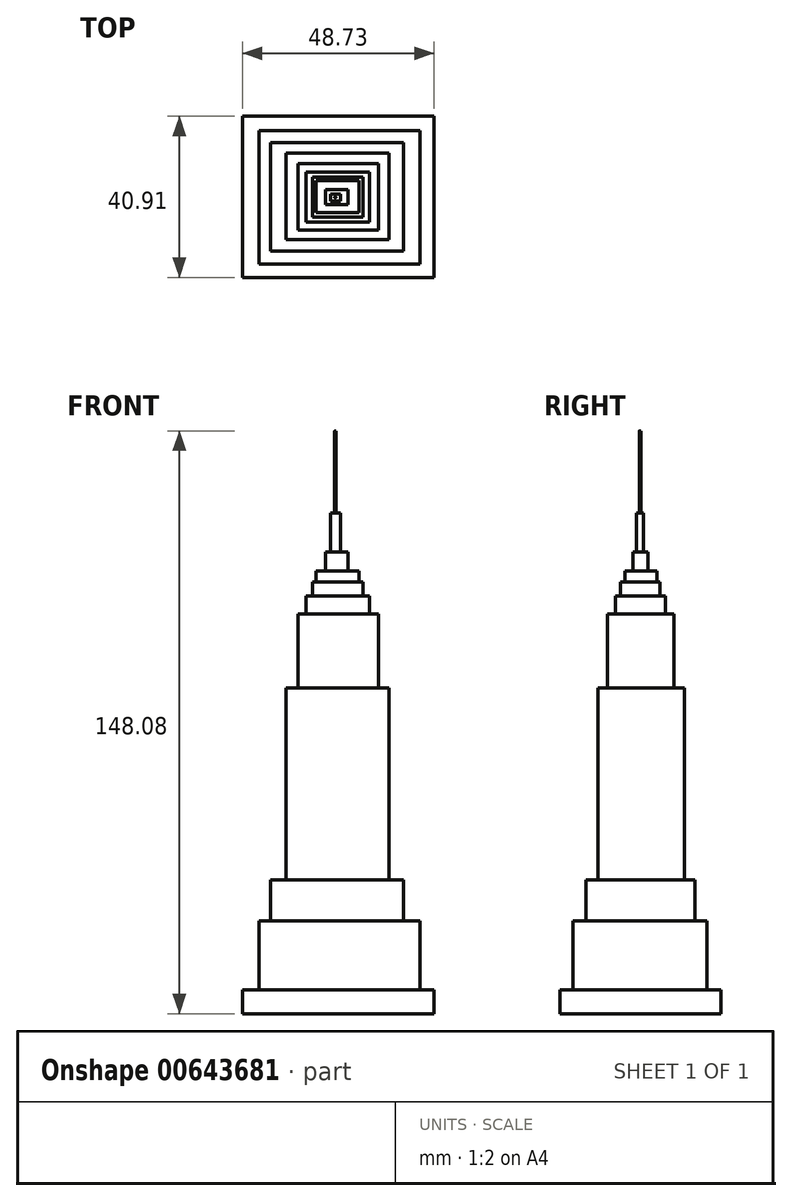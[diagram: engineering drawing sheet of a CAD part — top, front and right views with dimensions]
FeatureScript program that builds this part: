
annotation { "Feature Type Name" : "Feature", "Feature Type Description" : "" }
export const myFeature = defineFeature(function(context is Context, id is Id, definition is map)
    precondition{}
    {
        {
            var Q0;
            Q0=qCreatedBy(makeId("Top.planeOp"),FACE);
            var sketch = newSketch(context, id + "F0", { "sketchPlane" : qUnion([Q0])});
            skLineSegment(sketch, "E0.bottom", {"start": v(-23.61, 19.7) * mm, "end": v(25.12, 19.7) * mm});
            skLineSegment(sketch, "E0.top", {"start": v(-23.61, -21.2) * mm, "end": v(25.12, -21.2) * mm});
            skLineSegment(sketch, "E0.left", {"start": v(-23.61, 19.7) * mm, "end": v(-23.61, -21.2) * mm});
            skLineSegment(sketch, "E0.right", {"start": v(25.12, 19.7) * mm, "end": v(25.12, -21.2) * mm});
            skSolve(sketch);
        }
        {
            var Q0;
            Q0=makeQuery(id+"F0.imprint","IMPRINT",FACE,{"disambiguationData":[TD([[makeQuery(id+"F0.imprint","IMPRINT",EDGE,{"derivedFrom":sQuery(id+"F0.wireOp",EDGE,"E0.bottom")}),-1.0]])]});
            extrude(context, id + "F1", {"entities" : qUnion([Q0]), "depth" : 6.1 * mm, "offsetDistance" : 25.4 * mm});
        }
        {
            var Q0;
            Q0=makeQuery(id+"F1.opExtrude","CAP_FACE",FACE,{"disambiguationData":[OSD([sQuery(id+"F0.wireOp",EDGE,"E0.bottom"),sQuery(id+"F0.wireOp",EDGE,"E0.top"),sQuery(id+"F0.wireOp",EDGE,"E0.left"),sQuery(id+"F0.wireOp",EDGE,"E0.right")])],"isStart":false});
            var sketch = newSketch(context, id + "F2", { "sketchPlane" : qUnion([Q0])});
            skLineSegment(sketch, "E1.bottom", {"start": v(-19.4, 16.1) * mm, "end": v(21.5, 16.1) * mm});
            skLineSegment(sketch, "E1.top", {"start": v(-19.4, -17.9) * mm, "end": v(21.5, -17.9) * mm});
            skLineSegment(sketch, "E1.left", {"start": v(-19.4, 16.1) * mm, "end": v(-19.4, -17.9) * mm});
            skLineSegment(sketch, "E1.right", {"start": v(21.5, 16.1) * mm, "end": v(21.5, -17.9) * mm});
            skSolve(sketch);
        }
        {
            var Q0;
            Q0=makeQuery(id+"F2.imprint","IMPRINT",FACE,{"disambiguationData":[TD([[makeQuery(id+"F2.imprint","IMPRINT",EDGE,{"derivedFrom":sQuery(id+"F2.wireOp",EDGE,"E1.bottom")}),-1.0]])]});
            extrude(context, id + "F3", {"entities" : qUnion([Q0]), "depth" : 17.53 * mm, "offsetDistance" : 25.4 * mm});
        }
        {
            var Q0;
            Q0=makeQuery(id+"F3.opExtrude","CAP_FACE",FACE,{"disambiguationData":[OSD([sQuery(id+"F2.wireOp",EDGE,"E1.bottom"),sQuery(id+"F2.wireOp",EDGE,"E1.top"),sQuery(id+"F2.wireOp",EDGE,"E1.left"),sQuery(id+"F2.wireOp",EDGE,"E1.right")])],"isStart":false});
            var sketch = newSketch(context, id + "F4", { "sketchPlane" : qUnion([Q0])});
            skLineSegment(sketch, "E2.bottom", {"start": v(17.3, -14.59) * mm, "end": v(-16.4, -14.59) * mm});
            skLineSegment(sketch, "E2.top", {"start": v(17.3, 13.08) * mm, "end": v(-16.4, 13.08) * mm});
            skLineSegment(sketch, "E2.left", {"start": v(17.3, -14.59) * mm, "end": v(17.3, 13.08) * mm});
            skLineSegment(sketch, "E2.right", {"start": v(-16.4, -14.59) * mm, "end": v(-16.4, 13.08) * mm});
            skSolve(sketch);
        }
        {
            var Q0;
            Q0 = qSketchRegion(id + "F4", true);
            extrude(context, id + "F5", {"entities" : qUnion([Q0]), "depth" : 10.4 * mm, "offsetDistance" : 25.4 * mm});
        }
        {
            var Q0;
            Q0=makeQuery(id+"F5.opExtrude","CAP_FACE",FACE,{"disambiguationData":[OSD([sQuery(id+"F4.wireOp",EDGE,"E2.bottom"),sQuery(id+"F4.wireOp",EDGE,"E2.top"),sQuery(id+"F4.wireOp",EDGE,"E2.left"),sQuery(id+"F4.wireOp",EDGE,"E2.right")])],"isStart":false});
            var sketch = newSketch(context, id + "F6", { "sketchPlane" : qUnion([Q0])});
            skLineSegment(sketch, "E3.bottom", {"start": v(-12.48, 10.38) * mm, "end": v(13.69, 10.38) * mm});
            skLineSegment(sketch, "E3.top", {"start": v(-12.48, -11.58) * mm, "end": v(13.69, -11.58) * mm});
            skLineSegment(sketch, "E3.left", {"start": v(-12.48, 10.38) * mm, "end": v(-12.48, -11.58) * mm});
            skLineSegment(sketch, "E3.right", {"start": v(13.69, 10.38) * mm, "end": v(13.69, -11.58) * mm});
            skSolve(sketch);
        }
        {
            var Q0;
            Q0 = qSketchRegion(id + "F6", true);
            extrude(context, id + "F7", {"entities" : qUnion([Q0]), "depth" : 48.77 * mm, "offsetDistance" : 25.4 * mm});
        }
        {
            var Q0;
            Q0=makeQuery(id+"F7.opExtrude","CAP_FACE",FACE,{"disambiguationData":[OSD([sQuery(id+"F6.wireOp",EDGE,"E3.bottom"),sQuery(id+"F6.wireOp",EDGE,"E3.top"),sQuery(id+"F6.wireOp",EDGE,"E3.left"),sQuery(id+"F6.wireOp",EDGE,"E3.right")])],"isStart":false});
            var sketch = newSketch(context, id + "F8", { "sketchPlane" : qUnion([Q0])});
            skLineSegment(sketch, "E4.bottom", {"start": v(-9.47, 7.67) * mm, "end": v(10.98, 7.67) * mm});
            skLineSegment(sketch, "E4.top", {"start": v(-9.47, -9.17) * mm, "end": v(10.98, -9.17) * mm});
            skLineSegment(sketch, "E4.left", {"start": v(-9.47, 7.67) * mm, "end": v(-9.47, -9.17) * mm});
            skLineSegment(sketch, "E4.right", {"start": v(10.98, 7.67) * mm, "end": v(10.98, -9.17) * mm});
            skSolve(sketch);
        }
        {
            var Q0;
            Q0=makeQuery(id+"F8.imprint","IMPRINT",FACE,{"disambiguationData":[TD([[makeQuery(id+"F8.imprint","IMPRINT",EDGE,{"derivedFrom":sQuery(id+"F8.wireOp",EDGE,"E4.bottom")}),-1.0]])]});
            extrude(context, id + "F9", {"entities" : qUnion([Q0]), "depth" : 18.8 * mm, "offsetDistance" : 25.4 * mm});
        }
        {
            var Q0;
            Q0=makeQuery(id+"F9.opExtrude","CAP_FACE",FACE,{"disambiguationData":[OSD([sQuery(id+"F8.wireOp",EDGE,"E4.bottom"),sQuery(id+"F8.wireOp",EDGE,"E4.top"),sQuery(id+"F8.wireOp",EDGE,"E4.left"),sQuery(id+"F8.wireOp",EDGE,"E4.right")])],"isStart":false});
            var sketch = newSketch(context, id + "F10", { "sketchPlane" : qUnion([Q0])});
            skLineSegment(sketch, "E5.bottom", {"start": v(-7.47, 5.58) * mm, "end": v(8.75, 5.58) * mm});
            skLineSegment(sketch, "E5.top", {"start": v(-7.47, -7.1) * mm, "end": v(8.75, -7.1) * mm});
            skLineSegment(sketch, "E5.left", {"start": v(-7.47, 5.58) * mm, "end": v(-7.47, -7.1) * mm});
            skLineSegment(sketch, "E5.right", {"start": v(8.75, 5.58) * mm, "end": v(8.75, -7.1) * mm});
            skSolve(sketch);
        }
        {
            var Q0;
            Q0=makeQuery(id+"F10.imprint","IMPRINT",FACE,{"disambiguationData":[TD([[makeQuery(id+"F10.imprint","IMPRINT",EDGE,{"derivedFrom":sQuery(id+"F10.wireOp",EDGE,"E5.bottom")}),-1.0]])]});
            extrude(context, id + "F11", {"entities" : qUnion([Q0]), "depth" : 4.57 * mm, "offsetDistance" : 25.4 * mm});
        }
        {
            var Q0;
            Q0=makeQuery(id+"F11.opExtrude","CAP_FACE",FACE,{"disambiguationData":[OSD([sQuery(id+"F10.wireOp",EDGE,"E5.bottom"),sQuery(id+"F10.wireOp",EDGE,"E5.top"),sQuery(id+"F10.wireOp",EDGE,"E5.left"),sQuery(id+"F10.wireOp",EDGE,"E5.right")])],"isStart":false});
            var sketch = newSketch(context, id + "F12", { "sketchPlane" : qUnion([Q0])});
            skLineSegment(sketch, "E6.bottom", {"start": v(-5.71, 4.21) * mm, "end": v(7.07, 4.21) * mm});
            skLineSegment(sketch, "E6.top", {"start": v(-5.71, -5.87) * mm, "end": v(7.07, -5.87) * mm});
            skLineSegment(sketch, "E6.left", {"start": v(-5.71, 4.21) * mm, "end": v(-5.71, -5.87) * mm});
            skLineSegment(sketch, "E6.right", {"start": v(7.07, 4.21) * mm, "end": v(7.07, -5.87) * mm});
            skSolve(sketch);
        }
        {
            var Q0;
            Q0 = qSketchRegion(id + "F12", true);
            extrude(context, id + "F13", {"entities" : qUnion([Q0]), "depth" : 3.56 * mm, "offsetDistance" : 25.4 * mm});
        }
        {
            var Q0;
            Q0=makeQuery(id+"F13.opExtrude","CAP_FACE",FACE,{"disambiguationData":[OSD([sQuery(id+"F12.wireOp",EDGE,"E6.bottom"),sQuery(id+"F12.wireOp",EDGE,"E6.top"),sQuery(id+"F12.wireOp",EDGE,"E6.left"),sQuery(id+"F12.wireOp",EDGE,"E6.right")])],"isStart":false});
            var sketch = newSketch(context, id + "F14", { "sketchPlane" : qUnion([Q0])});
            skLineSegment(sketch, "E7.bottom", {"start": v(-4.9, 3.37) * mm, "end": v(6.06, 3.37) * mm});
            skLineSegment(sketch, "E7.top", {"start": v(-4.9, -4.72) * mm, "end": v(6.06, -4.72) * mm});
            skLineSegment(sketch, "E7.left", {"start": v(-4.9, 3.37) * mm, "end": v(-4.9, -4.72) * mm});
            skLineSegment(sketch, "E7.right", {"start": v(6.06, 3.37) * mm, "end": v(6.06, -4.72) * mm});
            skSolve(sketch);
        }
        {
            var Q0;
            Q0 = qSketchRegion(id + "F14", true);
            extrude(context, id + "F15", {"entities" : qUnion([Q0]), "depth" : 2.8 * mm, "offsetDistance" : 25.4 * mm});
        }
        {
            var Q0;
            Q0=makeQuery(id+"F15.opExtrude","CAP_FACE",FACE,{"disambiguationData":[OSD([sQuery(id+"F14.wireOp",EDGE,"E7.bottom"),sQuery(id+"F14.wireOp",EDGE,"E7.top"),sQuery(id+"F14.wireOp",EDGE,"E7.left"),sQuery(id+"F14.wireOp",EDGE,"E7.right")])],"isStart":false});
            var sketch = newSketch(context, id + "F16", { "sketchPlane" : qUnion([Q0])});
            skLineSegment(sketch, "E8.bottom", {"start": v(-2.5, 1.12) * mm, "end": v(3.19, 1.12) * mm});
            skLineSegment(sketch, "E8.top", {"start": v(-2.5, -2.67) * mm, "end": v(3.19, -2.67) * mm});
            skLineSegment(sketch, "E8.left", {"start": v(-2.5, 1.12) * mm, "end": v(-2.5, -2.67) * mm});
            skLineSegment(sketch, "E8.right", {"start": v(3.19, 1.12) * mm, "end": v(3.19, -2.67) * mm});
            skSolve(sketch);
        }
        {
            var Q0;
            Q0 = qSketchRegion(id + "F16", true);
            extrude(context, id + "F17", {"entities" : qUnion([Q0]), "depth" : 4.83 * mm, "offsetDistance" : 25.4 * mm});
        }
        {
            var Q0;
            Q0=makeQuery(id+"F17.opExtrude","CAP_FACE",FACE,{"disambiguationData":[OSD([sQuery(id+"F16.wireOp",EDGE,"E8.bottom"),sQuery(id+"F16.wireOp",EDGE,"E8.top"),sQuery(id+"F16.wireOp",EDGE,"E8.left"),sQuery(id+"F16.wireOp",EDGE,"E8.right")])],"isStart":false});
            var sketch = newSketch(context, id + "F18", { "sketchPlane" : qUnion([Q0])});
            skLineSegment(sketch, "E9.bottom", {"start": v(-1.14, 0) * mm, "end": v(1.32, 0) * mm});
            skLineSegment(sketch, "E9.top", {"start": v(-1.14, -1.86) * mm, "end": v(1.32, -1.86) * mm});
            skLineSegment(sketch, "E9.left", {"start": v(-1.14, 0) * mm, "end": v(-1.14, -1.86) * mm});
            skLineSegment(sketch, "E9.right", {"start": v(1.32, 0) * mm, "end": v(1.32, -1.86) * mm});
            skSolve(sketch);
        }
        {
            var Q0;
            Q0 = qSketchRegion(id + "F18", true);
            extrude(context, id + "F19", {"entities" : qUnion([Q0]), "depth" : 9.9 * mm, "offsetDistance" : 25.4 * mm});
        }
        {
            var Q0;
            Q0=makeQuery(id+"F19.opExtrude","CAP_FACE",FACE,{"disambiguationData":[OSD([sQuery(id+"F18.wireOp",EDGE,"E9.bottom"),sQuery(id+"F18.wireOp",EDGE,"E9.top"),sQuery(id+"F18.wireOp",EDGE,"E9.left"),sQuery(id+"F18.wireOp",EDGE,"E9.right")])],"isStart":false});
            var sketch = newSketch(context, id + "F20", { "sketchPlane" : qUnion([Q0])});
            skCircle(sketch, "E10", {"center": v(0, -0.89) * mm, "radius": 0.83 * mm});
            skSolve(sketch);
        }
        {
            var Q0;
            Q0=makeQuery(id+"F20.imprint","IMPRINT",FACE,{"disambiguationData":[TD([[makeQuery(id+"F20.imprint","IMPRINT",EDGE,{"derivedFrom":sQuery(id+"F20.wireOp",EDGE,"E10")}),1.0]])]});
            var sketch = newSketch(context, id + "F21", { "sketchPlane" : qUnion([Q0])});
            skCircle(sketch, "E11", {"center": v(0, -0.9) * mm, "radius": 0.16 * mm});
            skSolve(sketch);
        }
        {
            var Q0;
            Q0 = qSketchRegion(id + "F21", true);
            extrude(context, id + "F22", {"entities" : qUnion([Q0]), "depth" : 20.83 * mm, "offsetDistance" : 25.4 * mm});
        }
    });
